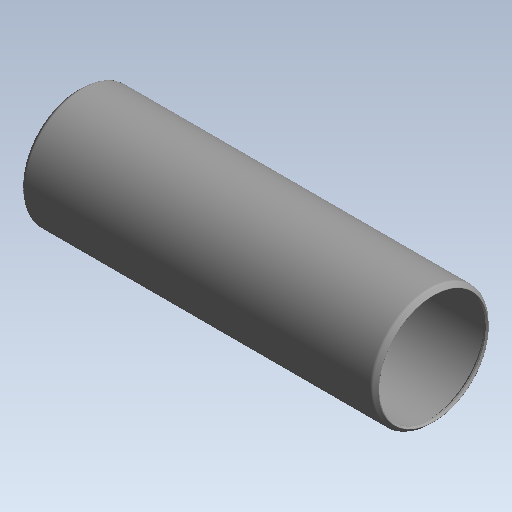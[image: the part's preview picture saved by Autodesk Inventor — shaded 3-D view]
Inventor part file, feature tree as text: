
AUTODESK INVENTOR PART (.ipt)
format: ipt  version: 2020 (Build 240168000, 168)  size: 144,384 bytes
history: native  units: mm (DEFAULTED — no unit token found)
features: other x42, revolve x1, sketch x1
ambient origin geometry x8: Origin, YZ Plane, XZ Plane, XY Plane, X Axis, Y Axis, Z Axis, Center Point
bodies: Solid1 (feature_tree)
feature tree (44):
  revolve  "Revolution1"  [1 undecoded]
  other  "cp1_XY"
  other  "cp1_YZ"
  other  "cp1_ZX"
  other  "cp1_X"
  other  "cp1_Y"
  other  "cp1_Z"
  other  "cp1_Center"
  other  "cp2_XY"
  other  "cp2_YZ"
  other  "cp2_ZX"
  other  "cp2_X"
  other  "cp2_Y"
  other  "cp2_Z"
  other  "cp2_Center"
  other  "cp3_XY"
  other  "cp3_YZ"
  other  "cp3_ZX"
  other  "cp3_X"
  other  "cp3_Y"
  other  "cp3_Z"
  other  "cp3_Center"
  other  "cp4_XY"
  other  "cp4_YZ"
  other  "cp4_ZX"
  other  "cp4_X"
  other  "cp4_Y"
  other  "cp4_Z"
  other  "cp4_Center"
  other  "tube_front_XY"
  other  "tube_front_YZ"
  other  "tube_front_ZX"
  other  "tube_front_X"
  other  "tube_front_Y"
  other  "tube_front_Z"
  other  "tube_front_Center"
  other  "tube_rear_XY"
  other  "tube_rear_YZ"
  other  "tube_rear_ZX"
  other  "tube_rear_X"
  other  "tube_rear_Y"
  other  "tube_rear_Z"
  other  "tube_rear_Center"
  sketch  "Sketch_1"  dims[d0=360.0deg]
note: 1 required parameter value undecoded (feature->parameter linkage not recoverable at this tier; creation-order binding heuristic only, values carry confidence <= 0.55)
